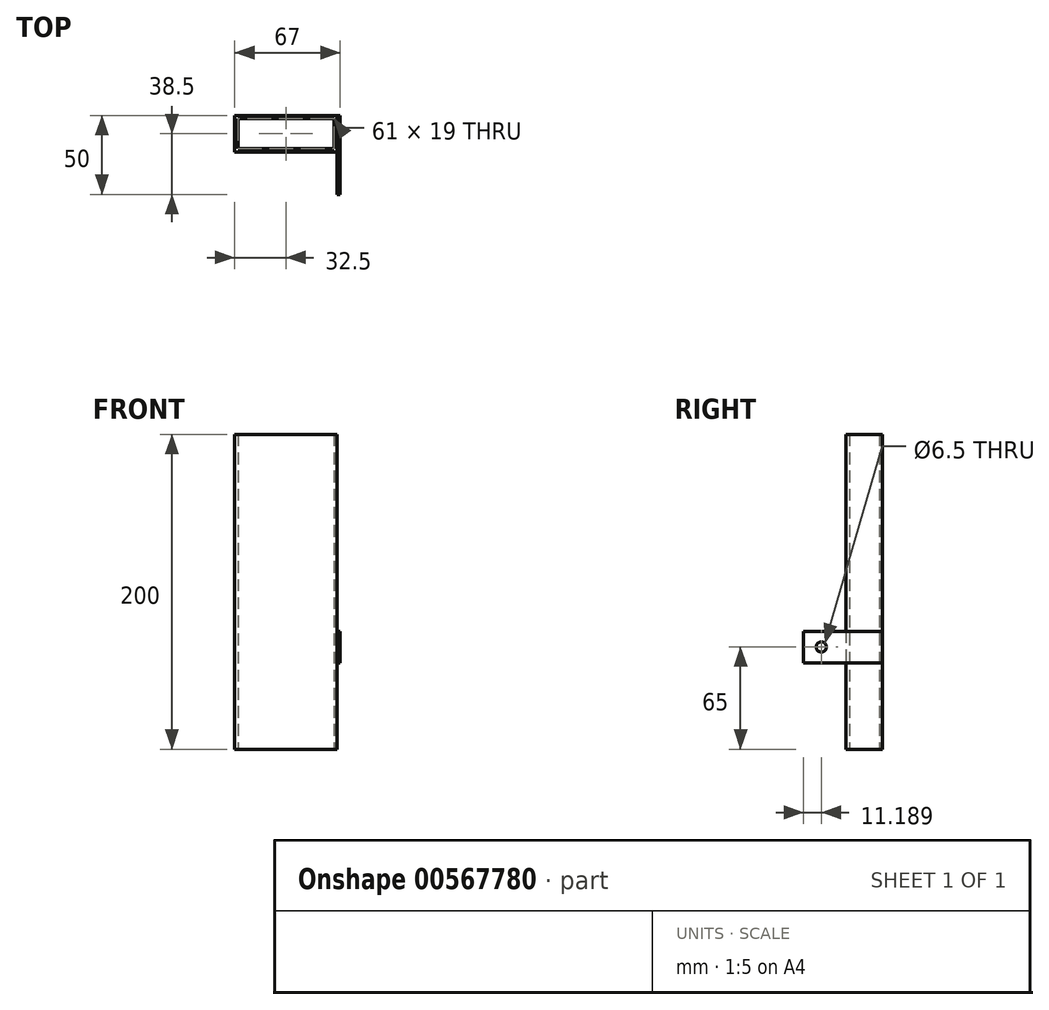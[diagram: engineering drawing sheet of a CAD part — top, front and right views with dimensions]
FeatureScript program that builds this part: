
annotation { "Feature Type Name" : "Feature", "Feature Type Description" : "" }
export const myFeature = defineFeature(function(context is Context, id is Id, definition is map)
    precondition{}
    {
        {
            var Q0;
            Q0=qCreatedBy(makeId("Front.planeOp"),FACE);
            var sketch = newSketch(context, id + "F0", { "sketchPlane" : qUnion([Q0])});
            skLineSegment(sketch, "E0.bottom", {"start": v(0, 0) * mm, "end": v(65, 0) * mm});
            skLineSegment(sketch, "E0.top", {"start": v(0, -200) * mm, "end": v(65, -200) * mm});
            skLineSegment(sketch, "E0.left", {"start": v(0, 0) * mm, "end": v(0, -200) * mm});
            skLineSegment(sketch, "E0.right", {"start": v(65, 0) * mm, "end": v(65, -200) * mm});
            skSolve(sketch);
        }
        {
            var Q0;
            Q0 = qSketchRegion(id + "F0", true);
            extrude(context, id + "F1", {"entities" : qUnion([Q0]), "oppositeDirection" : true, "depth" : 2 * mm, "offsetDistance" : 25 * mm});
        }
        {
            var Q0;
            Q0=makeQuery(id+"F1.opExtrude","SWEPT_FACE",FACE,{"disambiguationData":[OSD([sQuery(id+"F0.wireOp",EDGE,"E0.right")])]});
            var sketch = newSketch(context, id + "F2", { "sketchPlane" : qUnion([Q0])});
            skLineSegment(sketch, "E1.bottom", {"start": v(2, 0) * mm, "end": v(23, 0) * mm});
            skLineSegment(sketch, "E1.top", {"start": v(2, -200) * mm, "end": v(23, -200) * mm});
            skLineSegment(sketch, "E1.left", {"start": v(2, 0) * mm, "end": v(2, -200) * mm});
            skLineSegment(sketch, "E1.right", {"start": v(23, 0) * mm, "end": v(23, -200) * mm});
            skSolve(sketch);
        }
        {
            var Q0;
            Q0 = qSketchRegion(id + "F2", true);
            extrude(context, id + "F3", {"entities" : qUnion([Q0]), "operationType" : NewBodyOperationType.ADD, "oppositeDirection" : true, "depth" : 2 * mm, "offsetDistance" : 25 * mm});
        }
        {
            var Q0;
            Q0=makeQuery(id+"F3.opExtrude","SWEPT_FACE",FACE,{"disambiguationData":[OSD([sQuery(id+"F2.wireOp",EDGE,"E1.right")])]});
            var sketch = newSketch(context, id + "F4", { "sketchPlane" : qUnion([Q0])});
            skLineSegment(sketch, "E2.bottom", {"start": v(-63, 0) * mm, "end": v(0, 0) * mm});
            skLineSegment(sketch, "E2.top", {"start": v(-63, -200) * mm, "end": v(0, -200) * mm});
            skLineSegment(sketch, "E2.left", {"start": v(-63, 0) * mm, "end": v(-63, -200) * mm});
            skLineSegment(sketch, "E2.right", {"start": v(0, 0) * mm, "end": v(0, -200) * mm});
            skSolve(sketch);
        }
        {
            var Q0;
            Q0 = qSketchRegion(id + "F4", true);
            extrude(context, id + "F5", {"entities" : qUnion([Q0]), "operationType" : NewBodyOperationType.ADD, "oppositeDirection" : true, "depth" : 2 * mm, "offsetDistance" : 25 * mm});
        }
        {
            var Q0;
            Q0=makeQuery(id+"F5.opExtrude","SWEPT_FACE",FACE,{"disambiguationData":[OSD([sQuery(id+"F4.wireOp",EDGE,"E2.right")])]});
            var sketch = newSketch(context, id + "F6", { "sketchPlane" : qUnion([Q0])});
            skLineSegment(sketch, "E3.bottom", {"start": v(-21, 0) * mm, "end": v(-2, 0) * mm});
            skLineSegment(sketch, "E3.top", {"start": v(-21, -200) * mm, "end": v(-2, -200) * mm});
            skLineSegment(sketch, "E3.left", {"start": v(-21, 0) * mm, "end": v(-21, -200) * mm});
            skLineSegment(sketch, "E3.right", {"start": v(-2, 0) * mm, "end": v(-2, -200) * mm});
            skSolve(sketch);
        }
        {
            var Q0;
            Q0 = qSketchRegion(id + "F6", true);
            extrude(context, id + "F7", {"entities" : qUnion([Q0]), "operationType" : NewBodyOperationType.ADD, "oppositeDirection" : true, "depth" : 2 * mm, "offsetDistance" : 25 * mm});
        }
        {
            var Q0;
            Q0=makeQuery(id+"F3.boolean.opBoolean","MERGE",FACE,{"derivedFrom":[makeQuery(id+"F1.opExtrude","SWEPT_FACE",FACE,{"disambiguationData":[OSD([sQuery(id+"F0.wireOp",EDGE,"E0.right")])]}),makeQuery(id+"F3.opExtrude","CAP_FACE",FACE,{"disambiguationData":[OSD([sQuery(id+"F2.wireOp",EDGE,"E1.bottom"),sQuery(id+"F2.wireOp",EDGE,"E1.top"),sQuery(id+"F2.wireOp",EDGE,"E1.left"),sQuery(id+"F2.wireOp",EDGE,"E1.right")])],"isStart":true})]});
            var sketch = newSketch(context, id + "F8", { "sketchPlane" : qUnion([Q0])});
            skLineSegment(sketch, "E4.bottom", {"start": v(23, -145) * mm, "end": v(-27, -145) * mm});
            skLineSegment(sketch, "E4.top", {"start": v(23, -125) * mm, "end": v(-27, -125) * mm});
            skLineSegment(sketch, "E4.left", {"start": v(23, -145) * mm, "end": v(23, -125) * mm});
            skLineSegment(sketch, "E4.right", {"start": v(-27, -145) * mm, "end": v(-27, -125) * mm});
            skSolve(sketch);
        }
        {
            var Q0;
            {var subQ0=sQuery(id+"F8.wireOp",EDGE,"E4.left");Q0=makeQuery(id+"F8.imprint","IMPRINT",FACE,{"disambiguationData":[TD([[makeQuery(id+"F8.imprint","IMPRINT",EDGE,{"derivedFrom":subQ0}),-1.0]])]});}
            var Q1;
            {var subQ0=sQuery(id+"F8.wireOp",EDGE,"E4.right");Q1=makeQuery(id+"F8.imprint","IMPRINT",FACE,{"disambiguationData":[TD([[makeQuery(id+"F8.imprint","IMPRINT",EDGE,{"derivedFrom":subQ0}),-1.0]])]});}
            extrude(context, id + "F9", {"entities" : qUnion([Q0, Q1]), "operationType" : NewBodyOperationType.ADD, "depth" : 2 * mm, "offsetDistance" : 25 * mm});
        }
        {
            var Q0;
            Q0=makeQuery(id+"F9.opExtrude","CAP_FACE",FACE,{"disambiguationData":[OSD([sQuery(id+"F8.wireOp",EDGE,"E4.bottom"),sQuery(id+"F8.wireOp",EDGE,"E4.top"),sQuery(id+"F8.wireOp",EDGE,"E4.left"),sQuery(id+"F8.wireOp",EDGE,"E4.right")])],"isStart":false});
            var sketch = newSketch(context, id + "F10", { "sketchPlane" : qUnion([Q0])});
            skCircle(sketch, "E5", {"center": v(-15.81, -135) * mm, "radius": 3.25 * mm});
            skSolve(sketch);
        }
        {
            var Q0;
            Q0 = qSketchRegion(id + "F10", true);
            extrude(context, id + "F11", {"entities" : qUnion([Q0]), "operationType" : NewBodyOperationType.REMOVE, "oppositeDirection" : true, "depth" : 2 * mm, "offsetDistance" : 25 * mm});
        }
    });
